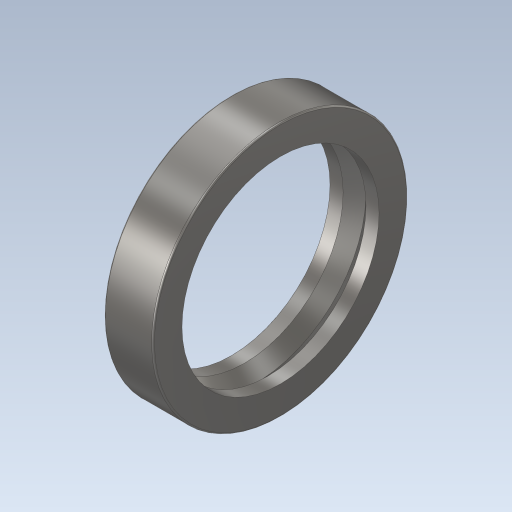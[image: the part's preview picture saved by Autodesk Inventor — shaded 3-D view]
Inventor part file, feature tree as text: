
AUTODESK INVENTOR PART (.ipt)
format: ipt  version: 2024 (Build 280153000, 153)  size: 172,032 bytes
history: native  units: mm
features: revolve x2, sketch x2
ambient origin geometry x8: Origin, YZ Plane, XZ Plane, XY Plane, X Axis, Y Axis, Z Axis, Center Point
bodies: Solid1 (feature_tree)
feature tree (4):
  revolve  "Revolution1"  Angle=360.0deg
  revolve  "Revolution2"  [1 undecoded]
  sketch  "Sketch_1"  dims[d0=360.0deg d1=360.0deg]
  sketch  "Sketch_4"
note: 1 required parameter value undecoded (feature->parameter linkage not recoverable at this tier; creation-order binding heuristic only, values carry confidence <= 0.55)
